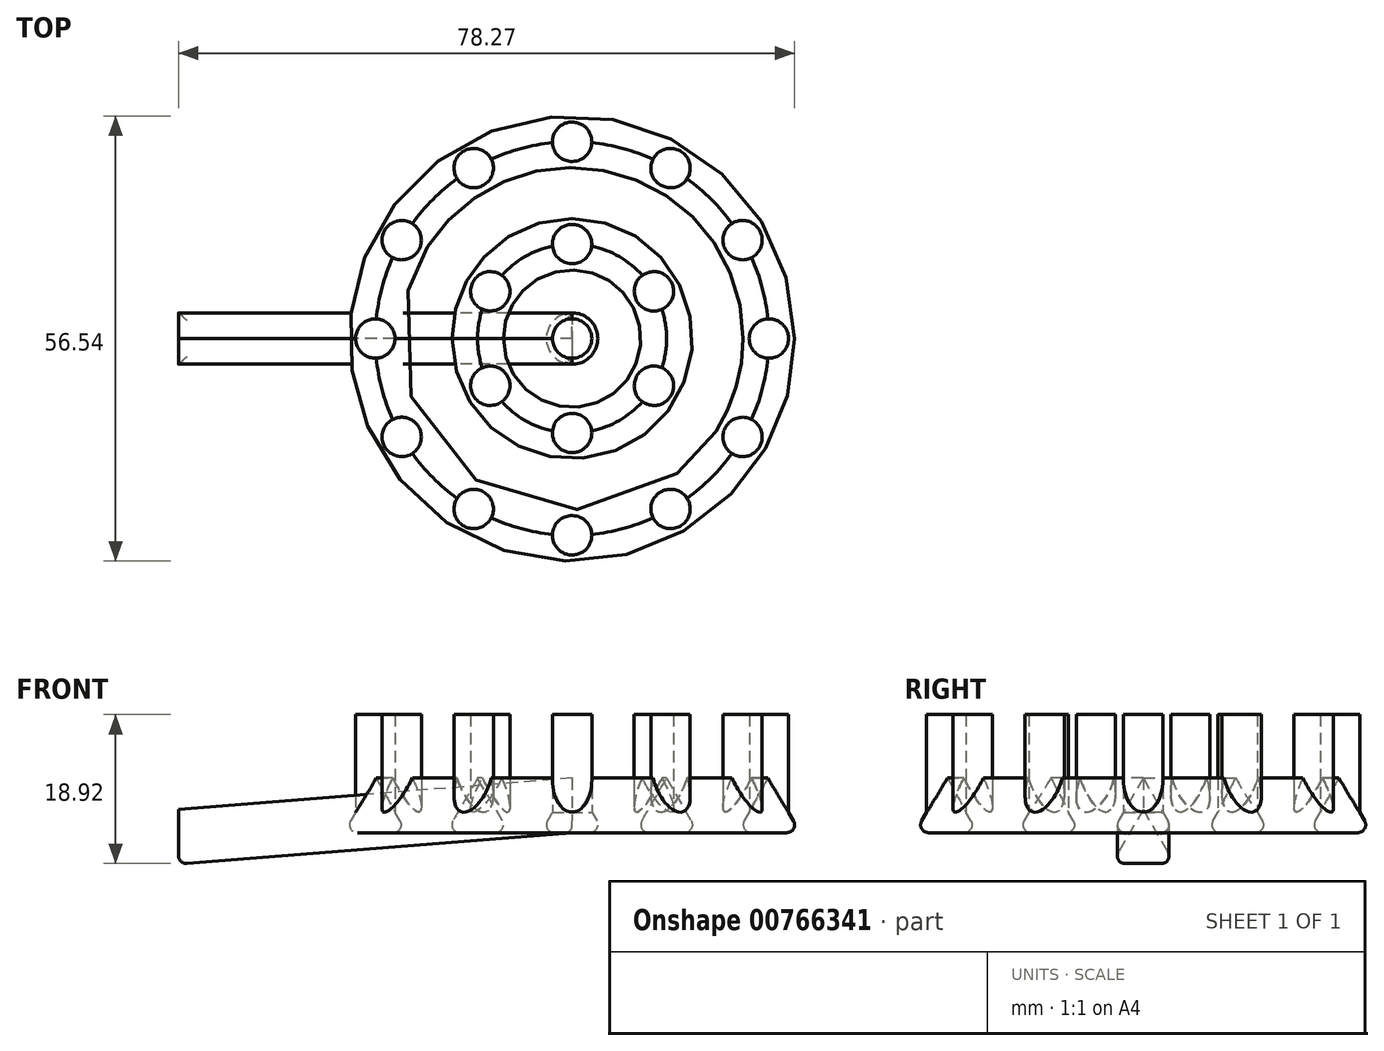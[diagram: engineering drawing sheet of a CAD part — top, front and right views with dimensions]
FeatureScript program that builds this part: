
annotation { "Feature Type Name" : "Feature", "Feature Type Description" : "" }
export const myFeature = defineFeature(function(context is Context, id is Id, definition is map)
    precondition{}
    {
        {
            var Q0;
            Q0=qCreatedBy(makeId("Top.planeOp"),FACE);
            var sketch = newSketch(context, id + "F0", { "sketchPlane" : qUnion([Q0])});
            skCircle(sketch, "E0", {"center": v(0, 0) * mm, "radius": 2.5 * mm});
            skCircle(sketch, "E1.1.0", {"center": v(12.5, 3.35) * mm, "radius": 2.5 * mm});
            skCircle(sketch, "E1.2.0", {"center": v(21.65, 12.5) * mm, "radius": 2.5 * mm});
            skPoint(sketch, "E1.center", {"position": v(0, 25) * mm});
            skCircle(sketch, "E2.1.3.0", {"center": v(25, 25) * mm, "radius": 2.5 * mm});
            skCircle(sketch, "E2.1.4.0", {"center": v(21.65, 37.5) * mm, "radius": 2.5 * mm});
            skCircle(sketch, "E2.1.5.0", {"center": v(12.5, 46.65) * mm, "radius": 2.5 * mm});
            skCircle(sketch, "E2.1.6.0", {"center": v(0, 50) * mm, "radius": 2.5 * mm});
            skCircle(sketch, "E2.1.7.0", {"center": v(-12.5, 46.65) * mm, "radius": 2.5 * mm});
            skCircle(sketch, "E2.1.8.0", {"center": v(-21.65, 37.5) * mm, "radius": 2.5 * mm});
            skCircle(sketch, "E2.1.9.0", {"center": v(-25, 25) * mm, "radius": 2.5 * mm});
            skCircle(sketch, "E2.1.10.0", {"center": v(-21.65, 12.5) * mm, "radius": 2.5 * mm});
            skCircle(sketch, "E2.1.11.0", {"center": v(-12.5, 3.35) * mm, "radius": 2.5 * mm});
            skLineSegment(sketch, "E3", {"start": v(0, 25) * mm, "end": v(0, 13) * mm, "construction": true});
            skCircle(sketch, "E4", {"center": v(0, 13) * mm, "radius": 2.5 * mm});
            skCircle(sketch, "E5", {"center": v(0, 25) * mm, "radius": 2.5 * mm});
            skCircle(sketch, "E6.1.0", {"center": v(10.4, 19) * mm, "radius": 2.5 * mm});
            skCircle(sketch, "E6.2.0", {"center": v(10.4, 31) * mm, "radius": 2.5 * mm});
            skCircle(sketch, "E6.3.0", {"center": v(0, 37) * mm, "radius": 2.5 * mm});
            skCircle(sketch, "E6.4.0", {"center": v(-10.4, 31) * mm, "radius": 2.5 * mm});
            skCircle(sketch, "E6.5.0", {"center": v(-10.4, 19) * mm, "radius": 2.5 * mm});
            skCircle(sketch, "E7", {"center": v(0, 25) * mm, "radius": 12 * mm});
            skCircle(sketch, "E8", {"center": v(0, 25) * mm, "radius": 25 * mm});
            skSolve(sketch);
        }
        {
            var Q0;
            Q0=qCreatedBy(makeId("Right.planeOp"),FACE);
            var sketch = newSketch(context, id + "F1", { "sketchPlane" : qUnion([Q0])});
            skLineSegment(sketch, "E9", {"start": v(-4, 0) * mm, "end": v(4, 0) * mm});
            skLineSegment(sketch, "E10", {"start": v(4, 0) * mm, "end": v(0, 6.93) * mm});
            skLineSegment(sketch, "E11", {"start": v(0, 6.93) * mm, "end": v(-4, 0) * mm});
            skLineSegment(sketch, "E12.1.0.0", {"start": v(25, 6.93) * mm, "end": v(21, 0) * mm});
            skLineSegment(sketch, "E12.direction1", {"start": v(-4, 0) * mm, "end": v(21, 0) * mm, "construction": true});
            skLineSegment(sketch, "E13.1.0.0", {"start": v(9, 0) * mm, "end": v(34, 0) * mm, "construction": true});
            skLineSegment(sketch, "E13.1.0.1", {"start": v(13, 6.93) * mm, "end": v(9, 0) * mm});
            skLineSegment(sketch, "E13.1.0.2", {"start": v(17, 0) * mm, "end": v(13, 6.93) * mm});
            skLineSegment(sketch, "E13.direction1", {"start": v(-4, 0) * mm, "end": v(9, 0) * mm, "construction": true});
            skLineSegment(sketch, "E14", {"start": v(25, 0) * mm, "end": v(25, 13.69) * mm});
            skLineSegment(sketch, "E15", {"start": v(21, 0) * mm, "end": v(25, 0) * mm});
            skLineSegment(sketch, "E16", {"start": v(17, 0) * mm, "end": v(9, 0) * mm});
            skLineSegment(sketch, "E17", {"start": v(25, 6.93) * mm, "end": v(29, 0) * mm});
            skLineSegment(sketch, "E18", {"start": v(29, 0) * mm, "end": v(25, 0) * mm});
            skSolve(sketch);
        }
        {
            var Q0;
            Q0=makeQuery(id+"F1.imprint","IMPRINT",FACE,{"disambiguationData":[TD([[makeQuery(id+"F1.imprint","IMPRINT",EDGE,{"derivedFrom":sQuery(id+"F1.wireOp",EDGE,"E13.1.0.1")}),1.0]])]});
            var Q1;
            Q1=makeQuery(id+"F1.imprint","IMPRINT",FACE,{"disambiguationData":[TD([[makeQuery(id+"F1.imprint","IMPRINT",EDGE,{"derivedFrom":sQuery(id+"F1.wireOp",EDGE,"E9")}),1.0]])]});
            var Q2;
            {var subQ0=sQuery(id+"F1.wireOp",EDGE,"E12.1.0.0");Q2=makeQuery(id+"F1.imprint","IMPRINT",FACE,{"disambiguationData":[TD([[makeQuery(id+"F1.imprint","IMPRINT",EDGE,{"derivedFrom":subQ0}),1.0]])]});}
            var Q3;
            Q3=sQuery(id+"F1.wireOp",EDGE,"E14");
            revolve(context, id + "F2", {"surfaceOperationType" : NewSurfaceOperationType.NEW, "entities" : qUnion([Q0, Q1, Q2]), "axis" : qUnion([Q3]), "revolveType" : RevolveType.FULL});
        }
        {
            var Q0;
            {var subQ0=sQuery(id+"F0.wireOp",EDGE,"E8");var subQ1=sQuery(id+"F0.wireOp",EDGE,"E2.1.11.0");var subQ2=makeQuery(id+"F0.imprint","INTERSECT",VERTEX,{"disambiguationData":[OD(0.0)],"derivedFrom":[subQ1,subQ0]});Q0=makeQuery(id+"F0.imprint","IMPRINT",FACE,{"disambiguationData":[TD([[makeQuery(id+"F0.imprint","IMPRINT",EDGE,{"disambiguationData":[TD([[subQ2,-1.0]])],"derivedFrom":subQ1}),1.0]])]});}
            var Q1;
            {var subQ0=sQuery(id+"F0.wireOp",EDGE,"E8");var subQ1=sQuery(id+"F0.wireOp",EDGE,"E2.1.11.0");var subQ2=makeQuery(id+"F0.imprint","INTERSECT",VERTEX,{"disambiguationData":[OD(0.0)],"derivedFrom":[subQ1,subQ0]});Q1=makeQuery(id+"F0.imprint","IMPRINT",FACE,{"disambiguationData":[TD([[makeQuery(id+"F0.imprint","IMPRINT",EDGE,{"disambiguationData":[TD([[subQ2,1.0]])],"derivedFrom":subQ1}),1.0]])]});}
            var Q2;
            {var subQ0=sQuery(id+"F0.wireOp",EDGE,"E8");var subQ1=sQuery(id+"F0.wireOp",EDGE,"E2.1.10.0");var subQ2=makeQuery(id+"F0.imprint","INTERSECT",VERTEX,{"disambiguationData":[OD(0.0)],"derivedFrom":[subQ1,subQ0]});Q2=makeQuery(id+"F0.imprint","IMPRINT",FACE,{"disambiguationData":[TD([[makeQuery(id+"F0.imprint","IMPRINT",EDGE,{"disambiguationData":[TD([[subQ2,-1.0]])],"derivedFrom":subQ1}),1.0]])]});}
            var Q3;
            {var subQ0=sQuery(id+"F0.wireOp",EDGE,"E8");var subQ1=sQuery(id+"F0.wireOp",EDGE,"E2.1.10.0");var subQ2=makeQuery(id+"F0.imprint","INTERSECT",VERTEX,{"disambiguationData":[OD(0.0)],"derivedFrom":[subQ1,subQ0]});Q3=makeQuery(id+"F0.imprint","IMPRINT",FACE,{"disambiguationData":[TD([[makeQuery(id+"F0.imprint","IMPRINT",EDGE,{"disambiguationData":[TD([[subQ2,1.0]])],"derivedFrom":subQ1}),1.0]])]});}
            var Q4;
            {var subQ0=sQuery(id+"F0.wireOp",EDGE,"E8");var subQ1=sQuery(id+"F0.wireOp",EDGE,"E2.1.9.0");var subQ2=makeQuery(id+"F0.imprint","INTERSECT",VERTEX,{"disambiguationData":[OD(0.0)],"derivedFrom":[subQ1,subQ0]});Q4=makeQuery(id+"F0.imprint","IMPRINT",FACE,{"disambiguationData":[TD([[makeQuery(id+"F0.imprint","IMPRINT",EDGE,{"disambiguationData":[TD([[subQ2,-1.0]])],"derivedFrom":subQ1}),1.0]])]});}
            var Q5;
            {var subQ0=sQuery(id+"F0.wireOp",EDGE,"E8");var subQ1=sQuery(id+"F0.wireOp",EDGE,"E2.1.9.0");var subQ2=makeQuery(id+"F0.imprint","INTERSECT",VERTEX,{"disambiguationData":[OD(0.0)],"derivedFrom":[subQ1,subQ0]});Q5=makeQuery(id+"F0.imprint","IMPRINT",FACE,{"disambiguationData":[TD([[makeQuery(id+"F0.imprint","IMPRINT",EDGE,{"disambiguationData":[TD([[subQ2,1.0]])],"derivedFrom":subQ1}),1.0]])]});}
            var Q6;
            {var subQ0=sQuery(id+"F0.wireOp",EDGE,"E8");var subQ1=sQuery(id+"F0.wireOp",EDGE,"E2.1.8.0");var subQ2=makeQuery(id+"F0.imprint","INTERSECT",VERTEX,{"disambiguationData":[OD(0.0)],"derivedFrom":[subQ1,subQ0]});Q6=makeQuery(id+"F0.imprint","IMPRINT",FACE,{"disambiguationData":[TD([[makeQuery(id+"F0.imprint","IMPRINT",EDGE,{"disambiguationData":[TD([[subQ2,1.0]])],"derivedFrom":subQ1}),1.0]])]});}
            var Q7;
            {var subQ0=sQuery(id+"F0.wireOp",EDGE,"E8");var subQ1=sQuery(id+"F0.wireOp",EDGE,"E2.1.8.0");var subQ2=makeQuery(id+"F0.imprint","INTERSECT",VERTEX,{"disambiguationData":[OD(0.0)],"derivedFrom":[subQ1,subQ0]});Q7=makeQuery(id+"F0.imprint","IMPRINT",FACE,{"disambiguationData":[TD([[makeQuery(id+"F0.imprint","IMPRINT",EDGE,{"disambiguationData":[TD([[subQ2,-1.0]])],"derivedFrom":subQ1}),1.0]])]});}
            var Q8;
            {var subQ0=sQuery(id+"F0.wireOp",EDGE,"E8");var subQ1=sQuery(id+"F0.wireOp",EDGE,"E2.1.7.0");var subQ2=makeQuery(id+"F0.imprint","INTERSECT",VERTEX,{"disambiguationData":[OD(0.0)],"derivedFrom":[subQ1,subQ0]});Q8=makeQuery(id+"F0.imprint","IMPRINT",FACE,{"disambiguationData":[TD([[makeQuery(id+"F0.imprint","IMPRINT",EDGE,{"disambiguationData":[TD([[subQ2,-1.0]])],"derivedFrom":subQ1}),1.0]])]});}
            var Q9;
            {var subQ0=sQuery(id+"F0.wireOp",EDGE,"E8");var subQ1=sQuery(id+"F0.wireOp",EDGE,"E2.1.7.0");var subQ2=makeQuery(id+"F0.imprint","INTERSECT",VERTEX,{"disambiguationData":[OD(0.0)],"derivedFrom":[subQ1,subQ0]});Q9=makeQuery(id+"F0.imprint","IMPRINT",FACE,{"disambiguationData":[TD([[makeQuery(id+"F0.imprint","IMPRINT",EDGE,{"disambiguationData":[TD([[subQ2,1.0]])],"derivedFrom":subQ1}),1.0]])]});}
            var Q10;
            {var subQ0=sQuery(id+"F0.wireOp",EDGE,"E8");var subQ1=sQuery(id+"F0.wireOp",EDGE,"E2.1.6.0");var subQ2=makeQuery(id+"F0.imprint","INTERSECT",VERTEX,{"disambiguationData":[OD(0.0)],"derivedFrom":[subQ1,subQ0]});Q10=makeQuery(id+"F0.imprint","IMPRINT",FACE,{"disambiguationData":[TD([[makeQuery(id+"F0.imprint","IMPRINT",EDGE,{"disambiguationData":[TD([[subQ2,-1.0]])],"derivedFrom":subQ1}),1.0]])]});}
            var Q11;
            {var subQ0=sQuery(id+"F0.wireOp",EDGE,"E8");var subQ1=sQuery(id+"F0.wireOp",EDGE,"E2.1.5.0");var subQ2=makeQuery(id+"F0.imprint","INTERSECT",VERTEX,{"disambiguationData":[OD(0.0)],"derivedFrom":[subQ1,subQ0]});Q11=makeQuery(id+"F0.imprint","IMPRINT",FACE,{"disambiguationData":[TD([[makeQuery(id+"F0.imprint","IMPRINT",EDGE,{"disambiguationData":[TD([[subQ2,-1.0]])],"derivedFrom":subQ1}),1.0]])]});}
            var Q12;
            {var subQ0=sQuery(id+"F0.wireOp",EDGE,"E8");var subQ1=sQuery(id+"F0.wireOp",EDGE,"E2.1.4.0");var subQ2=makeQuery(id+"F0.imprint","INTERSECT",VERTEX,{"disambiguationData":[OD(0.0)],"derivedFrom":[subQ1,subQ0]});Q12=makeQuery(id+"F0.imprint","IMPRINT",FACE,{"disambiguationData":[TD([[makeQuery(id+"F0.imprint","IMPRINT",EDGE,{"disambiguationData":[TD([[subQ2,1.0]])],"derivedFrom":subQ1}),1.0]])]});}
            var Q13;
            {var subQ0=sQuery(id+"F0.wireOp",EDGE,"E8");var subQ1=sQuery(id+"F0.wireOp",EDGE,"E0");var subQ2=makeQuery(id+"F0.imprint","INTERSECT",VERTEX,{"disambiguationData":[OD(0.0)],"derivedFrom":[subQ1,subQ0]});Q13=makeQuery(id+"F0.imprint","IMPRINT",FACE,{"disambiguationData":[TD([[makeQuery(id+"F0.imprint","IMPRINT",EDGE,{"disambiguationData":[TD([[subQ2,1.0]])],"derivedFrom":subQ1}),1.0]])]});}
            var Q14;
            {var subQ0=sQuery(id+"F0.wireOp",EDGE,"E8");var subQ1=sQuery(id+"F0.wireOp",EDGE,"E1.1.0");var subQ2=makeQuery(id+"F0.imprint","INTERSECT",VERTEX,{"disambiguationData":[OD(0.0)],"derivedFrom":[subQ1,subQ0]});Q14=makeQuery(id+"F0.imprint","IMPRINT",FACE,{"disambiguationData":[TD([[makeQuery(id+"F0.imprint","IMPRINT",EDGE,{"disambiguationData":[TD([[subQ2,-1.0]])],"derivedFrom":subQ1}),1.0]])]});}
            var Q15;
            {var subQ0=sQuery(id+"F0.wireOp",EDGE,"E8");var subQ1=sQuery(id+"F0.wireOp",EDGE,"E1.1.0");var subQ2=makeQuery(id+"F0.imprint","INTERSECT",VERTEX,{"disambiguationData":[OD(0.0)],"derivedFrom":[subQ1,subQ0]});Q15=makeQuery(id+"F0.imprint","IMPRINT",FACE,{"disambiguationData":[TD([[makeQuery(id+"F0.imprint","IMPRINT",EDGE,{"disambiguationData":[TD([[subQ2,1.0]])],"derivedFrom":subQ1}),1.0]])]});}
            var Q16;
            {var subQ0=sQuery(id+"F0.wireOp",EDGE,"E8");var subQ1=sQuery(id+"F0.wireOp",EDGE,"E1.2.0");var subQ2=makeQuery(id+"F0.imprint","INTERSECT",VERTEX,{"disambiguationData":[OD(0.0)],"derivedFrom":[subQ1,subQ0]});Q16=makeQuery(id+"F0.imprint","IMPRINT",FACE,{"disambiguationData":[TD([[makeQuery(id+"F0.imprint","IMPRINT",EDGE,{"disambiguationData":[TD([[subQ2,-1.0]])],"derivedFrom":subQ1}),1.0]])]});}
            var Q17;
            {var subQ0=sQuery(id+"F0.wireOp",EDGE,"E8");var subQ1=sQuery(id+"F0.wireOp",EDGE,"E1.2.0");var subQ2=makeQuery(id+"F0.imprint","INTERSECT",VERTEX,{"disambiguationData":[OD(0.0)],"derivedFrom":[subQ1,subQ0]});Q17=makeQuery(id+"F0.imprint","IMPRINT",FACE,{"disambiguationData":[TD([[makeQuery(id+"F0.imprint","IMPRINT",EDGE,{"disambiguationData":[TD([[subQ2,1.0]])],"derivedFrom":subQ1}),1.0]])]});}
            var Q18;
            {var subQ0=sQuery(id+"F0.wireOp",EDGE,"E8");var subQ1=sQuery(id+"F0.wireOp",EDGE,"E2.1.3.0");var subQ2=makeQuery(id+"F0.imprint","INTERSECT",VERTEX,{"disambiguationData":[OD(0.0)],"derivedFrom":[subQ1,subQ0]});Q18=makeQuery(id+"F0.imprint","IMPRINT",FACE,{"disambiguationData":[TD([[makeQuery(id+"F0.imprint","IMPRINT",EDGE,{"disambiguationData":[TD([[subQ2,1.0]])],"derivedFrom":subQ1}),1.0]])]});}
            var Q19;
            {var subQ0=sQuery(id+"F0.wireOp",EDGE,"E8");var subQ1=sQuery(id+"F0.wireOp",EDGE,"E2.1.3.0");var subQ2=makeQuery(id+"F0.imprint","INTERSECT",VERTEX,{"disambiguationData":[OD(0.0)],"derivedFrom":[subQ1,subQ0]});Q19=makeQuery(id+"F0.imprint","IMPRINT",FACE,{"disambiguationData":[TD([[makeQuery(id+"F0.imprint","IMPRINT",EDGE,{"disambiguationData":[TD([[subQ2,-1.0]])],"derivedFrom":subQ1}),1.0]])]});}
            var Q20;
            {var subQ0=sQuery(id+"F0.wireOp",EDGE,"E7");var subQ1=sQuery(id+"F0.wireOp",EDGE,"E6.1.0");var subQ2=makeQuery(id+"F0.imprint","INTERSECT",VERTEX,{"disambiguationData":[OD(0.0)],"derivedFrom":[subQ1,subQ0]});Q20=makeQuery(id+"F0.imprint","IMPRINT",FACE,{"disambiguationData":[TD([[makeQuery(id+"F0.imprint","IMPRINT",EDGE,{"disambiguationData":[TD([[subQ2,-1.0]])],"derivedFrom":subQ1}),1.0]])]});}
            var Q21;
            {var subQ0=sQuery(id+"F0.wireOp",EDGE,"E7");var subQ1=sQuery(id+"F0.wireOp",EDGE,"E6.1.0");var subQ2=makeQuery(id+"F0.imprint","INTERSECT",VERTEX,{"disambiguationData":[OD(0.0)],"derivedFrom":[subQ1,subQ0]});Q21=makeQuery(id+"F0.imprint","IMPRINT",FACE,{"disambiguationData":[TD([[makeQuery(id+"F0.imprint","IMPRINT",EDGE,{"disambiguationData":[TD([[subQ2,1.0]])],"derivedFrom":subQ1}),1.0]])]});}
            var Q22;
            {var subQ0=sQuery(id+"F0.wireOp",EDGE,"E7");var subQ1=sQuery(id+"F0.wireOp",EDGE,"E6.2.0");var subQ2=makeQuery(id+"F0.imprint","INTERSECT",VERTEX,{"disambiguationData":[OD(0.0)],"derivedFrom":[subQ1,subQ0]});Q22=makeQuery(id+"F0.imprint","IMPRINT",FACE,{"disambiguationData":[TD([[makeQuery(id+"F0.imprint","IMPRINT",EDGE,{"disambiguationData":[TD([[subQ2,1.0]])],"derivedFrom":subQ1}),1.0]])]});}
            var Q23;
            {var subQ0=sQuery(id+"F0.wireOp",EDGE,"E7");var subQ1=sQuery(id+"F0.wireOp",EDGE,"E6.3.0");var subQ2=makeQuery(id+"F0.imprint","INTERSECT",VERTEX,{"disambiguationData":[OD(0.0)],"derivedFrom":[subQ1,subQ0]});Q23=makeQuery(id+"F0.imprint","IMPRINT",FACE,{"disambiguationData":[TD([[makeQuery(id+"F0.imprint","IMPRINT",EDGE,{"disambiguationData":[TD([[subQ2,1.0]])],"derivedFrom":subQ1}),1.0]])]});}
            var Q24;
            {var subQ0=sQuery(id+"F0.wireOp",EDGE,"E7");var subQ1=sQuery(id+"F0.wireOp",EDGE,"E6.3.0");var subQ2=makeQuery(id+"F0.imprint","INTERSECT",VERTEX,{"disambiguationData":[OD(0.0)],"derivedFrom":[subQ1,subQ0]});Q24=makeQuery(id+"F0.imprint","IMPRINT",FACE,{"disambiguationData":[TD([[makeQuery(id+"F0.imprint","IMPRINT",EDGE,{"disambiguationData":[TD([[subQ2,-1.0]])],"derivedFrom":subQ1}),1.0]])]});}
            var Q25;
            Q25=makeQuery(id+"F0.imprint","IMPRINT",FACE,{"disambiguationData":[TD([[makeQuery(id+"F0.imprint","IMPRINT",EDGE,{"derivedFrom":sQuery(id+"F0.wireOp",EDGE,"E5")}),1.0]])]});
            var Q26;
            {var subQ0=sQuery(id+"F0.wireOp",EDGE,"E7");var subQ1=sQuery(id+"F0.wireOp",EDGE,"E6.2.0");var subQ2=makeQuery(id+"F0.imprint","INTERSECT",VERTEX,{"disambiguationData":[OD(0.0)],"derivedFrom":[subQ1,subQ0]});Q26=makeQuery(id+"F0.imprint","IMPRINT",FACE,{"disambiguationData":[TD([[makeQuery(id+"F0.imprint","IMPRINT",EDGE,{"disambiguationData":[TD([[subQ2,-1.0]])],"derivedFrom":subQ1}),1.0]])]});}
            var Q27;
            {var subQ0=sQuery(id+"F0.wireOp",EDGE,"E7");var subQ1=sQuery(id+"F0.wireOp",EDGE,"E4");var subQ2=makeQuery(id+"F0.imprint","INTERSECT",VERTEX,{"disambiguationData":[OD(0.0)],"derivedFrom":[subQ1,subQ0]});Q27=makeQuery(id+"F0.imprint","IMPRINT",FACE,{"disambiguationData":[TD([[makeQuery(id+"F0.imprint","IMPRINT",EDGE,{"disambiguationData":[TD([[subQ2,-1.0]])],"derivedFrom":subQ1}),1.0]])]});}
            var Q28;
            {var subQ0=sQuery(id+"F0.wireOp",EDGE,"E7");var subQ1=sQuery(id+"F0.wireOp",EDGE,"E6.5.0");var subQ2=makeQuery(id+"F0.imprint","INTERSECT",VERTEX,{"disambiguationData":[OD(0.0)],"derivedFrom":[subQ1,subQ0]});Q28=makeQuery(id+"F0.imprint","IMPRINT",FACE,{"disambiguationData":[TD([[makeQuery(id+"F0.imprint","IMPRINT",EDGE,{"disambiguationData":[TD([[subQ2,-1.0]])],"derivedFrom":subQ1}),1.0]])]});}
            var Q29;
            {var subQ0=sQuery(id+"F0.wireOp",EDGE,"E7");var subQ1=sQuery(id+"F0.wireOp",EDGE,"E6.5.0");var subQ2=makeQuery(id+"F0.imprint","INTERSECT",VERTEX,{"disambiguationData":[OD(0.0)],"derivedFrom":[subQ1,subQ0]});Q29=makeQuery(id+"F0.imprint","IMPRINT",FACE,{"disambiguationData":[TD([[makeQuery(id+"F0.imprint","IMPRINT",EDGE,{"disambiguationData":[TD([[subQ2,1.0]])],"derivedFrom":subQ1}),1.0]])]});}
            var Q30;
            {var subQ0=sQuery(id+"F0.wireOp",EDGE,"E7");var subQ1=sQuery(id+"F0.wireOp",EDGE,"E4");var subQ2=makeQuery(id+"F0.imprint","INTERSECT",VERTEX,{"disambiguationData":[OD(0.0)],"derivedFrom":[subQ1,subQ0]});Q30=makeQuery(id+"F0.imprint","IMPRINT",FACE,{"disambiguationData":[TD([[makeQuery(id+"F0.imprint","IMPRINT",EDGE,{"disambiguationData":[TD([[subQ2,1.0]])],"derivedFrom":subQ1}),1.0]])]});}
            var Q31;
            {var subQ0=sQuery(id+"F0.wireOp",EDGE,"E7");var subQ1=sQuery(id+"F0.wireOp",EDGE,"E6.4.0");var subQ2=makeQuery(id+"F0.imprint","INTERSECT",VERTEX,{"disambiguationData":[OD(0.0)],"derivedFrom":[subQ1,subQ0]});Q31=makeQuery(id+"F0.imprint","IMPRINT",FACE,{"disambiguationData":[TD([[makeQuery(id+"F0.imprint","IMPRINT",EDGE,{"disambiguationData":[TD([[subQ2,1.0]])],"derivedFrom":subQ1}),1.0]])]});}
            var Q32;
            {var subQ0=sQuery(id+"F0.wireOp",EDGE,"E7");var subQ1=sQuery(id+"F0.wireOp",EDGE,"E6.4.0");var subQ2=makeQuery(id+"F0.imprint","INTERSECT",VERTEX,{"disambiguationData":[OD(0.0)],"derivedFrom":[subQ1,subQ0]});Q32=makeQuery(id+"F0.imprint","IMPRINT",FACE,{"disambiguationData":[TD([[makeQuery(id+"F0.imprint","IMPRINT",EDGE,{"disambiguationData":[TD([[subQ2,-1.0]])],"derivedFrom":subQ1}),1.0]])]});}
            var Q33;
            {var subQ0=sQuery(id+"F0.wireOp",EDGE,"E8");var subQ1=sQuery(id+"F0.wireOp",EDGE,"E0");var subQ2=makeQuery(id+"F0.imprint","INTERSECT",VERTEX,{"disambiguationData":[OD(0.0)],"derivedFrom":[subQ1,subQ0]});Q33=makeQuery(id+"F0.imprint","IMPRINT",FACE,{"disambiguationData":[TD([[makeQuery(id+"F0.imprint","IMPRINT",EDGE,{"disambiguationData":[TD([[subQ2,-1.0]])],"derivedFrom":subQ1}),1.0]])]});}
            var Q34;
            {var subQ0=sQuery(id+"F0.wireOp",EDGE,"E8");var subQ1=sQuery(id+"F0.wireOp",EDGE,"E2.1.6.0");var subQ2=makeQuery(id+"F0.imprint","INTERSECT",VERTEX,{"disambiguationData":[OD(0.0)],"derivedFrom":[subQ1,subQ0]});Q34=makeQuery(id+"F0.imprint","IMPRINT",FACE,{"disambiguationData":[TD([[makeQuery(id+"F0.imprint","IMPRINT",EDGE,{"disambiguationData":[TD([[subQ2,1.0]])],"derivedFrom":subQ1}),1.0]])]});}
            var Q35;
            {var subQ0=sQuery(id+"F0.wireOp",EDGE,"E8");var subQ1=sQuery(id+"F0.wireOp",EDGE,"E2.1.4.0");var subQ2=makeQuery(id+"F0.imprint","INTERSECT",VERTEX,{"disambiguationData":[OD(0.0)],"derivedFrom":[subQ1,subQ0]});Q35=makeQuery(id+"F0.imprint","IMPRINT",FACE,{"disambiguationData":[TD([[makeQuery(id+"F0.imprint","IMPRINT",EDGE,{"disambiguationData":[TD([[subQ2,-1.0]])],"derivedFrom":subQ1}),1.0]])]});}
            var Q36;
            {var subQ0=sQuery(id+"F0.wireOp",EDGE,"E8");var subQ1=sQuery(id+"F0.wireOp",EDGE,"E2.1.5.0");var subQ2=makeQuery(id+"F0.imprint","INTERSECT",VERTEX,{"disambiguationData":[OD(0.0)],"derivedFrom":[subQ1,subQ0]});Q36=makeQuery(id+"F0.imprint","IMPRINT",FACE,{"disambiguationData":[TD([[makeQuery(id+"F0.imprint","IMPRINT",EDGE,{"disambiguationData":[TD([[subQ2,1.0]])],"derivedFrom":subQ1}),1.0]])]});}
            extrude(context, id + "F3", {"entities" : qUnion([Q0, Q1, Q2, Q3, Q4, Q5, Q6, Q7, Q8, Q9, Q10, Q11, Q12, Q13, Q14, Q15, Q16, Q17, Q18, Q19, Q20, Q21, Q22, Q23, Q24, Q25, Q26, Q27, Q28, Q29, Q30, Q31, Q32, Q33, Q34, Q35, Q36]), "operationType" : NewBodyOperationType.ADD, "depth" : 15 * mm, "offsetDistance" : 25 * mm});
        }
        {
            var Q0;
            Q0=qCreatedBy(makeId("Front.planeOp"),FACE);
            var sketch = newSketch(context, id + "F4", { "sketchPlane" : qUnion([Q0])});
            skLineSegment(sketch, "E19", {"start": v(0, 0) * mm, "end": v(-50, -4) * mm});
            skSolve(sketch);
        }
        {
            var Q0;
            {var subQ0=sQuery(id+"F1.wireOp",EDGE,"E17");Q0=makeQuery(id+"F1.imprint","IMPRINT",FACE,{"disambiguationData":[TD([[makeQuery(id+"F1.imprint","IMPRINT",EDGE,{"derivedFrom":subQ0}),-1.0]])]});}
            var Q1;
            {var subQ0=sQuery(id+"F1.wireOp",EDGE,"E12.1.0.0");Q1=makeQuery(id+"F1.imprint","IMPRINT",FACE,{"disambiguationData":[TD([[makeQuery(id+"F1.imprint","IMPRINT",EDGE,{"derivedFrom":subQ0}),1.0]])]});}
            var Q2;
            Q2=sQuery(id+"F4.wireOp",EDGE,"E19");
            sweep(context, id + "F5", {"profiles" : qUnion([Q0, Q1]), "path" : qUnion([Q2])});
        }
        {
            var Q0;
            Q0=makeQuery(id+"F2.opRevolve","SWEPT_FACE",FACE,{"disambiguationData":[OSD([sQuery(id+"F1.wireOp",EDGE,"E9")])]});
            var Q1;
            Q1=makeQuery(id+"F2.opRevolve","SWEPT_FACE",FACE,{"disambiguationData":[OSD([sQuery(id+"F1.wireOp",EDGE,"E16")])]});
            var Q2;
            Q2=makeQuery(id+"F5.opSweep","SWEPT_FACE",FACE,{"disambiguationData":[OSD([sQuery(id+"F1.wireOp",EDGE,"E15"),sQuery(id+"F1.wireOp",EDGE,"E18"),sQuery(id+"F4.wireOp",EDGE,"E19")])]});
            var Q3;
            Q3=makeQuery(id+"F2.opRevolve","SWEPT_FACE",FACE,{"disambiguationData":[OSD([sQuery(id+"F1.wireOp",EDGE,"E15")])]});
            fillet(context, id + "F6", {"entities" : qUnion([Q0, Q1, Q2, Q3]), "radius" : 1 * mm, "tangentPropagation" : true, "allowEdgeOverflow" : false});
        }
    });
